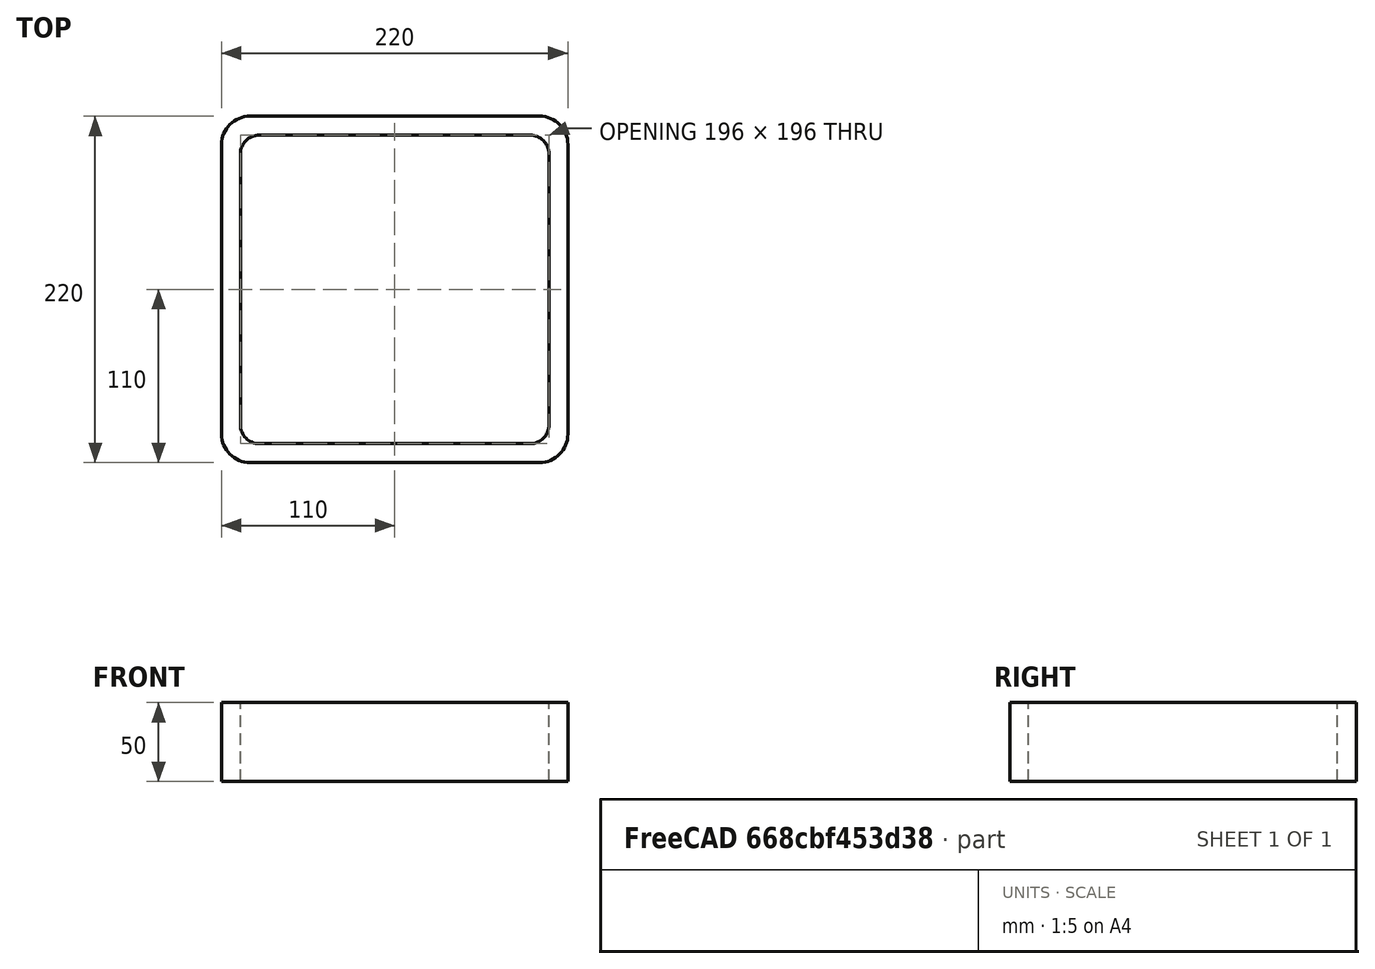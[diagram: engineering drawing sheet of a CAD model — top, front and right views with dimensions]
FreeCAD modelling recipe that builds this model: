
FCSTD DOCUMENT  (FreeCAD 0.15R4671 (Git))
Label: Square hollow section 220x220x12 EN10219 S235JRH
License: All rights reserved
LicenseURL: http://en.wikipedia.org/wiki/All_rights_reserved
objects: Sketcher::SketchObject×1, Part::Extrusion×1
note: 2 computed .brp shape members not serialized (recipe doc carries the construction recipe); baked Part::Feature solids carry a one-line shape summary decoded from their .brp

FEATURE [Sketcher::SketchObject] Sketch
  sketch-geometry (16):
    g0: LineSegment StartX=-86 StartY=98 StartZ=0 EndX=86 EndY=98 EndZ=0
    g1: LineSegment StartX=98 StartY=86 StartZ=0 EndX=98 EndY=-86 EndZ=0
    g2: LineSegment StartX=86 StartY=-98 StartZ=0 EndX=-86 EndY=-98 EndZ=0
    g3: LineSegment StartX=-98 StartY=-86 StartZ=0 EndX=-98 EndY=86 EndZ=0
    g4: LineSegment StartX=-92 StartY=110 StartZ=0 EndX=92 EndY=110 EndZ=0
    g5: LineSegment StartX=110 StartY=92 StartZ=0 EndX=110 EndY=-92 EndZ=0
    g6: LineSegment StartX=92 StartY=-110 StartZ=0 EndX=-92 EndY=-110 EndZ=0
    g7: LineSegment StartX=-110 StartY=-92 StartZ=0 EndX=-110 EndY=92 EndZ=0
    g8: ArcOfCircle CenterX=-86 CenterY=86 CenterZ=0 NormalX=0 NormalY=0 NormalZ=1 Radius=12 StartAngle=1.5708 EndAngle=3.14159
    g9: ArcOfCircle CenterX=86 CenterY=86 CenterZ=0 NormalX=0 NormalY=0 NormalZ=1 Radius=12 StartAngle=0 EndAngle=1.5708
    g10: ArcOfCircle CenterX=86 CenterY=-86 CenterZ=0 NormalX=0 NormalY=0 NormalZ=1 Radius=12 StartAngle=4.71239 EndAngle=6.28319
    g11: ArcOfCircle CenterX=-86 CenterY=-86 CenterZ=0 NormalX=0 NormalY=0 NormalZ=1 Radius=12 StartAngle=3.14159 EndAngle=4.71239
    g12: ArcOfCircle CenterX=92 CenterY=92 CenterZ=0 NormalX=0 NormalY=0 NormalZ=1 Radius=18 StartAngle=0 EndAngle=1.5708
    g13: ArcOfCircle CenterX=92 CenterY=-92 CenterZ=0 NormalX=0 NormalY=0 NormalZ=1 Radius=18 StartAngle=4.71239 EndAngle=6.28319
    g14: ArcOfCircle CenterX=-92 CenterY=-92 CenterZ=0 NormalX=0 NormalY=0 NormalZ=1 Radius=18 StartAngle=3.14159 EndAngle=4.71239
    g15: ArcOfCircle CenterX=-92 CenterY=92 CenterZ=0 NormalX=0 NormalY=0 NormalZ=1 Radius=18 StartAngle=1.5708 EndAngle=3.14159
  constraints (36):
    c: Horizontal(g2)
    c: Vertical(g3)
    c: Horizontal(g6)
    c: Vertical(g7)
    c: Tangent(g3,g8) = 1.5708
    c: Tangent(g0,g8) = 1.5708
    c: Tangent(g0,g9) = 1.5708
    c: Tangent(g1,g9) = 1.5708
    c: Tangent(g1,g10) = 1.5708
    c: Tangent(g2,g10) = 1.5708
    c: Tangent(g2,g11) = 1.5708
    c: Tangent(g3,g11) = 1.5708
    c: Tangent(g4,g12) = 1.5708
    c: Tangent(g5,g12) = 1.5708
    c: Tangent(g5,g13) = 1.5708
    c: Tangent(g6,g13) = 1.5708
    c: Tangent(g6,g14) = 1.5708
    c: Tangent(g7,g14) = 1.5708
    c: Tangent(g7,g15) = 1.5708
    c: Tangent(g4,g15) = 1.5708
    c: Equal(g9,g8)
    c: Equal(g9,g11)
    c: Equal(g9,g10)
    c: Equal(g12,g15)
    c: Equal(g12,g14)
    c: Equal(g12,g13)
    c: Symmetric(g4,g6,g-1)
    c: Symmetric(g7,g5,g-2)
    c: DistanceY(g4,g6) = -220
    c: DistanceX(g7,g5) = 220
    c: Symmetric(g3,g1,g-2)
    c: Symmetric(g0,g2,g-1)
    c: DistanceY(g0,g4) = 12
    c: DistanceX(g5,g1) = -12
    c: Radius(g9) = 12
    c: Radius(g12) = 18
FEATURE [Part::Extrusion] Extrude  label="Square hollow section 220x220x12 EN10219 S235JRH"
  Base = -> Sketch
  Dir = (0,0,50)
  Solid = true
